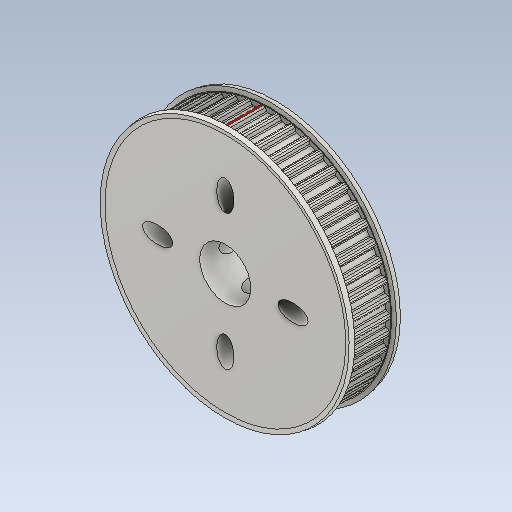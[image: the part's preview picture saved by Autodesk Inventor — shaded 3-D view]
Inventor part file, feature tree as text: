
AUTODESK INVENTOR PART (.ipt)
format: ipt  version: 2020 (Build 240168000, 168)  size: 764,416 bytes
history: native  units: mm (DEFAULTED — no unit token found)
features: other x6, extrude x3, sketch x3, pattern_circular x2, hole x2, fillet x1, plane x1, reference x1
ambient origin geometry x8: Origin, YZ Plane, XZ Plane, XY Plane, X Axis, Y Axis, Z Axis, Center Point
bodies: Solid1 (feature_tree)
feature tree (19):
  other  "Pulley Sketch"
  extrude  "Base Body"  Depth=0.3mm
  extrude  "Tooth"  Depth=8.726646mm
  fillet  "Tooth Fillet"  Radius=1.05mm
  pattern_circular  "Teeth"  [2 undecoded]
  other  "Left flange"
  other  "Right flange"
  hole  "Hole1"  [1 undecoded]
  extrude  "Extrusion3"  TaperAngle=0.0deg  [1 undecoded]
  plane  "Work Plane3"
  hole  "Hole2"  [1 undecoded]
  pattern_circular  "Circular Pattern2"  [2 undecoded]
  sketch  "Sketch2"  dims[d0=39.788736mm d1=0.3mm]
  sketch  "Sketch3"  dims[d2=0.75mm d3=8.726646mm d4=1.05mm]
  reference  "Reference1"
  sketch  "Sketch9"  dims[d5=6.5mm d6=0.0mm d7=6.5mm d8=0.0mm d9=0.2mm d10=0.3mm d11=500.0mm d12=360.0deg d15=0.0mm d16=0.0mm d17=8.3mm d18=6.0mm d19=3.023mm d20=2.0mm d21=14.3117mm d22=8.0mm d23=0.0mm d24=11.0mm d25=2.0mm d26=0.0mm d32=3.0mm d33=2.8mm d34=6.0mm d35=3.023mm d36=2.0mm d37=14.3117mm d38=15.0mm d39=0.0mm d40=40.0mm d41=360.0deg]
  parser-record x1  (decoder bookkeeping rows leaked as tree rows — omitted from the tree; the rows remain in map.json)
  other  "10-03-00 AnsambluZ_V2.iam"
  other  "ISO 1224-1 (Metric) 18 - 8 x 16 x 4:1"
note: 7 required parameter values undecoded (feature->parameter linkage not recoverable at this tier; creation-order binding heuristic only, values carry confidence <= 0.55)
note: 1 file-system path scrubbed to <path> (originals preserved in map.json)
